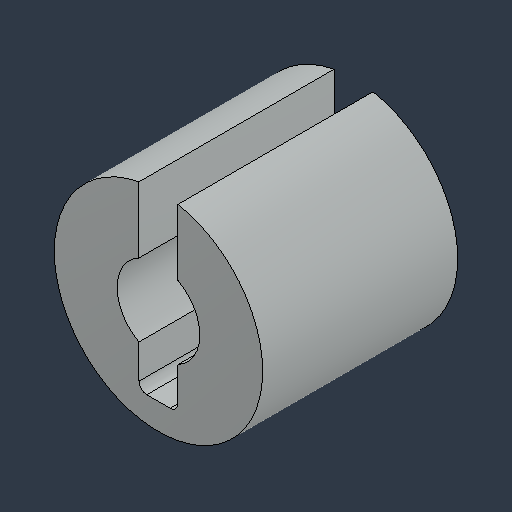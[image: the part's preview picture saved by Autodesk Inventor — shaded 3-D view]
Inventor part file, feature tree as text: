
AUTODESK INVENTOR PART (.ipt)
format: ipt  version: 2024.3 (Build 283343000, 343)  size: 113,152 bytes
history: native  units: in
note: dims shown in document units (in); Inventor stores cm internally (conversion verified against a paired STEP export)
features: fillet x1
ambient origin geometry x8: Origin, YZ Plane, XZ Plane, XY Plane, X Axis, Y Axis, Z Axis, Center Point
bodies: Solid1 (feature_tree)
feature tree (1):
  fillet  "Fillet1"  [1 undecoded]
note: 1 required parameter value undecoded (feature->parameter linkage not recoverable at this tier; creation-order binding heuristic only, values carry confidence <= 0.55)
